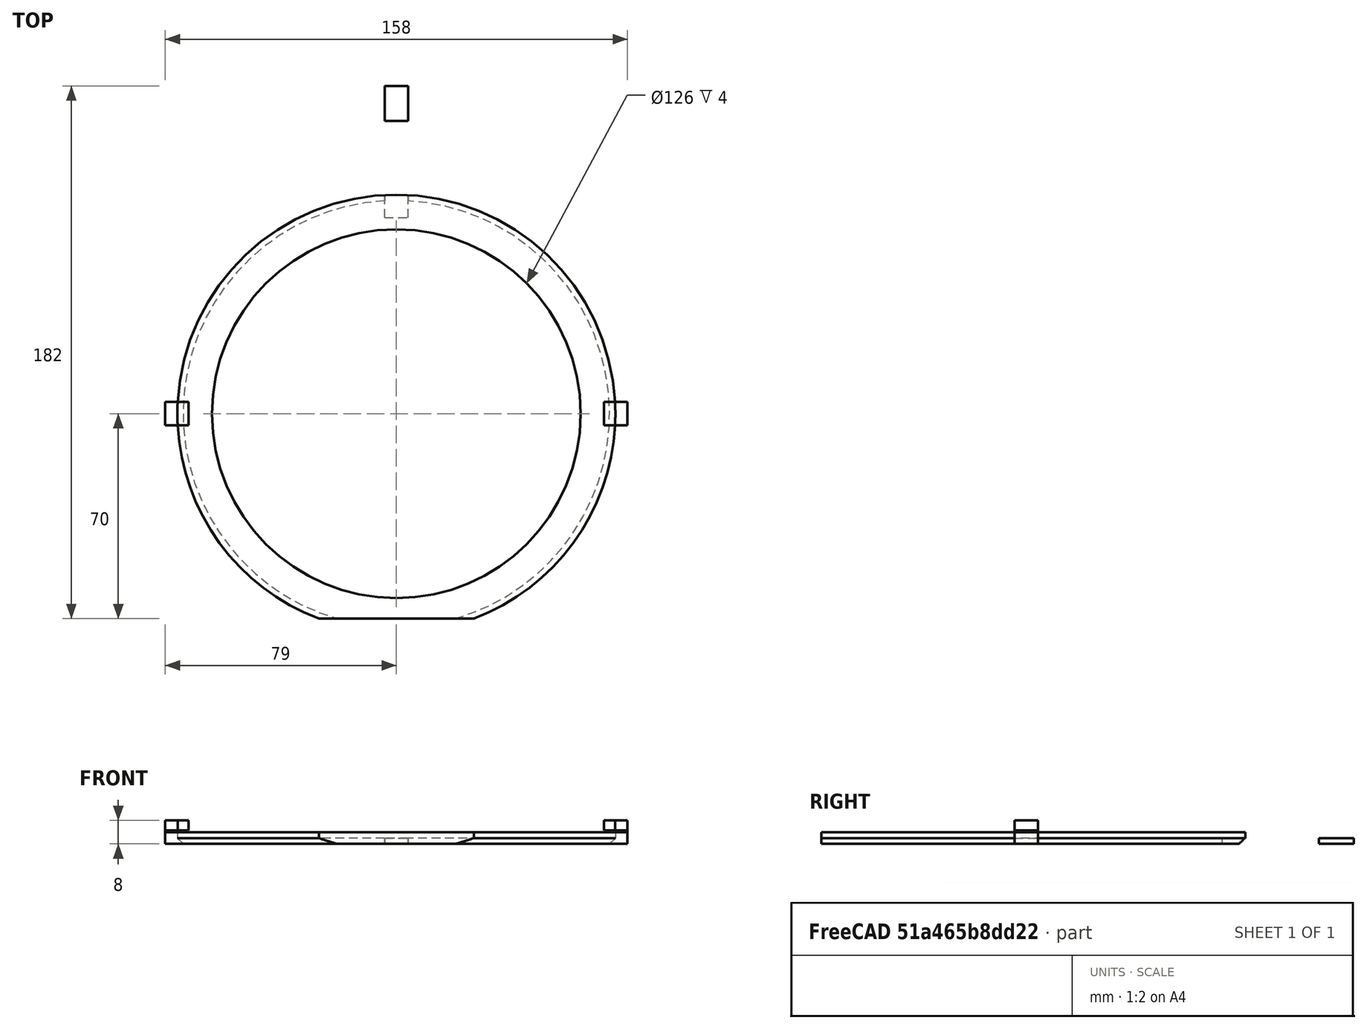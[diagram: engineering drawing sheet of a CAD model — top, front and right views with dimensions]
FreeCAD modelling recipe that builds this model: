
FCSTD DOCUMENT  (FreeCAD 0.19R0.19.2)
Label: waferHolder_005
License: All rights reserved
LicenseURL: http://en.wikipedia.org/wiki/All_rights_reserved
objects: Part::Box×8, Sketcher::SketchObject×2, Part::Extrusion×2, Part::Cut×2, Part::Chamfer×1, Part::MultiFuse×1
note: 16 computed .brp shape members not serialized (recipe doc carries the construction recipe); baked Part::Feature solids carry a one-line shape summary decoded from their .brp

FEATURE [Sketcher::SketchObject] Sketch
  FullyConstrained = true
  sketch-geometry (3):
    g0: Circle CenterX=-3.1415e-12 CenterY=5.6243e-12 CenterZ=0 NormalX=0 NormalY=0 NormalZ=1 AngleXU=0 Radius=63
    g1: ArcOfCircle CenterX=-3.1415e-12 CenterY=5.6243e-12 CenterZ=0 NormalX=0 NormalY=0 NormalZ=1 AngleXU=0 Radius=74.8482 StartAngle=5.07429 EndAngle=10.6337
    g2: LineSegment StartX=-26.5 StartY=-70.0001 StartZ=0 EndX=26.5 EndY=-70.0001 EndZ=0
  constraints (6):
    c: Block(g0)
    c: Coincident(g1,g0)
    c: Block(g1)
    c: Coincident(g2,g1)
    c: Coincident(g2,g1)
    c: Horizontal(g2)
FEATURE [Part::Box] Box  label="holderBitLeft"
  AttacherType = Attacher::AttachEngine3D
  Height = 4
  Length = 8
  Placement = pos=(-79,-4,0) rot=(0,0,1;0rad)
  Width = 8
FEATURE [Part::Box] Box001  label="bitHolderTopCutout"
  AttacherType = Attacher::AttachEngine3D
  Height = 4
  Length = 8
  Placement = pos=(-4,67,-2) rot=(0,0,1;0rad)
  Width = 12
FEATURE [Part::Extrusion] Extrude  label="mainHolderRing"
  Base = -> Sketch
  Dir = (0,0,1)
  DirMode = 2
  FaceMakerClass = Part::FaceMakerBullseye
  LengthFwd = 4
  LengthRev = 0
  Solid = true
  Symmetric = false
FEATURE [Part::Box] Box002  label="holderBitRight"
  AttacherType = Attacher::AttachEngine3D
  Height = 4
  Length = 8
  Placement = pos=(71,-4,0) rot=(0,0,1;0rad)
  Width = 8
FEATURE [Part::Box] Box003  label="bitHolderTop"
  AttacherType = Attacher::AttachEngine3D
  Height = 2
  Length = 8
  Placement = pos=(-4,100,0) rot=(0,0,1;0rad)
  Width = 12
FEATURE [Part::Chamfer] Chamfer
  Base = -> Extrude
  Edges = 1 edges r=2: [Edge3]
FEATURE [Part::Cut] Cut  label="mainHolderRing001"
  Base = -> Chamfer
  Tool = -> Box001
FEATURE [Part::Box] Box004  label="holderBitLeft001"
  AttacherType = Attacher::AttachEngine3D
  Height = 4
  Length = 6
  Placement = pos=(-79,-4,0) rot=(0,0,1;0rad)
  Width = 8
FEATURE [Part::Box] Box005  label="holderBitright002"
  AttacherType = Attacher::AttachEngine3D
  Height = 4
  Length = 6
  Placement = pos=(73,-4,0) rot=(0,0,1;0rad)
  Width = 8
FEATURE [Part::MultiFuse] Fusion  label="holders"
  Shapes = -> [Box004,Box005]
FEATURE [Sketcher::SketchObject] Sketch001
  FullyConstrained = true
  sketch-geometry (3):
    g0: Circle CenterX=-3.1415e-12 CenterY=5.6243e-12 CenterZ=0 NormalX=0 NormalY=0 NormalZ=1 AngleXU=0 Radius=63
    g1: ArcOfCircle CenterX=-3.1415e-12 CenterY=5.6243e-12 CenterZ=0 NormalX=0 NormalY=0 NormalZ=1 AngleXU=0 Radius=74.8482 StartAngle=5.07429 EndAngle=10.6337
    g2: LineSegment StartX=-26.5 StartY=-70.0001 StartZ=0 EndX=26.5 EndY=-70.0001 EndZ=0
  constraints (6):
    c: Block(g0)
    c: Coincident(g1,g0)
    c: Block(g1)
    c: Coincident(g2,g1)
    c: Coincident(g2,g1)
    c: Horizontal(g2)
FEATURE [Part::Extrusion] Extrude001  label="mainHolderRing002"
  Base = -> Sketch001
  Dir = (0,0,1)
  DirMode = 2
  FaceMakerClass = Part::FaceMakerBullseye
  LengthFwd = 4
  LengthRev = 0
  Solid = true
  Symmetric = false
FEATURE [Part::Cut] Cut001
  Base = -> Fusion
  Placement = pos=(0,0,4) rot=(0,0,1;0rad)
  Tool = -> Extrude001
FEATURE [Part::Box] Box006  label="holderBitRight001"
  AttacherType = Attacher::AttachEngine3D
  Height = 3.4
  Length = 8
  Placement = pos=(-79,-4,4.6) rot=(0,0,1;0rad)
  Width = 8
FEATURE [Part::Box] Box007  label="holderBitRight002"
  AttacherType = Attacher::AttachEngine3D
  Height = 3.4
  Length = 8
  Placement = pos=(71,-4,4.6) rot=(0,0,1;0rad)
  Width = 8
